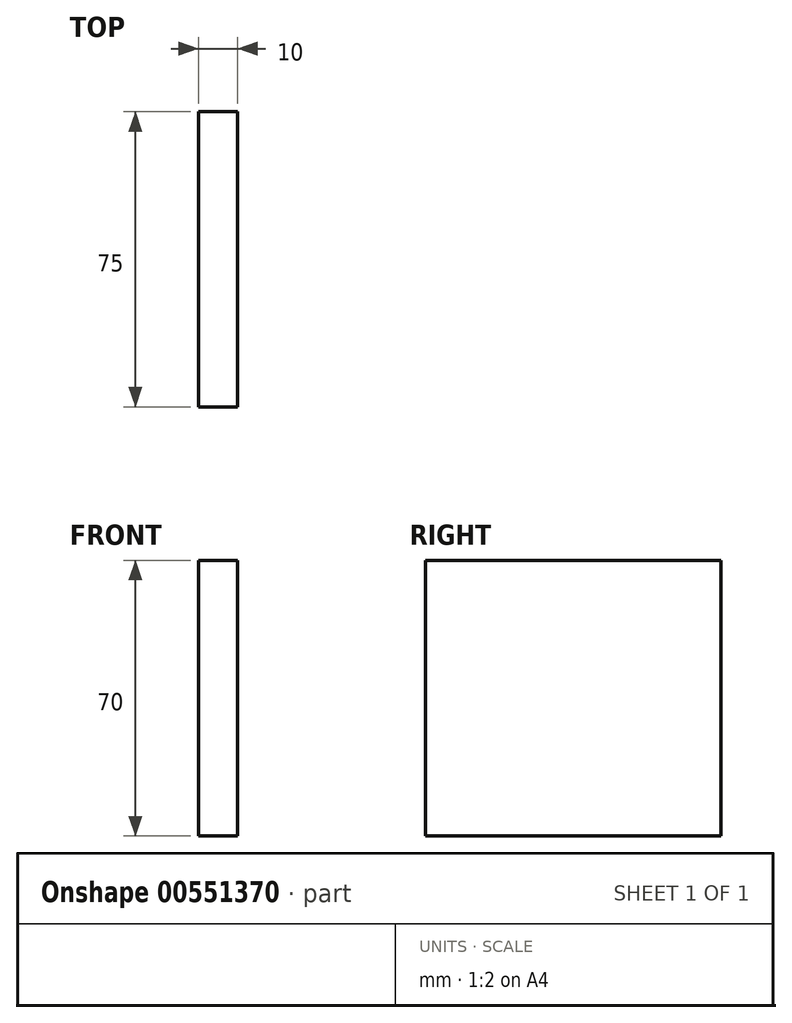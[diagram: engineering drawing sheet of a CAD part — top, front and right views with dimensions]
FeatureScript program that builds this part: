
annotation { "Feature Type Name" : "Feature", "Feature Type Description" : "" }
export const myFeature = defineFeature(function(context is Context, id is Id, definition is map)
    precondition{}
    {
        {
            var Q0;
            Q0=qCreatedBy(makeId("Right.planeOp"),FACE);
            var sketch = newSketch(context, id + "F0", { "sketchPlane" : qUnion([Q0])});
            skLineSegment(sketch, "E0.bottom", {"start": v(-39.57, 61.23) * mm, "end": v(35.43, 61.23) * mm});
            skLineSegment(sketch, "E0.top", {"start": v(-39.57, -8.77) * mm, "end": v(35.43, -8.77) * mm});
            skLineSegment(sketch, "E0.left", {"start": v(-39.57, 61.23) * mm, "end": v(-39.57, -8.77) * mm});
            skLineSegment(sketch, "E0.right", {"start": v(35.43, 61.23) * mm, "end": v(35.43, -8.77) * mm});
            skSolve(sketch);
        }
        {
            var Q0;
            Q0 = qSketchRegion(id + "F0", true);
            extrude(context, id + "F1", {"entities" : qUnion([Q0]), "depth" : 10 * mm, "offsetDistance" : 25 * mm});
        }
    });
